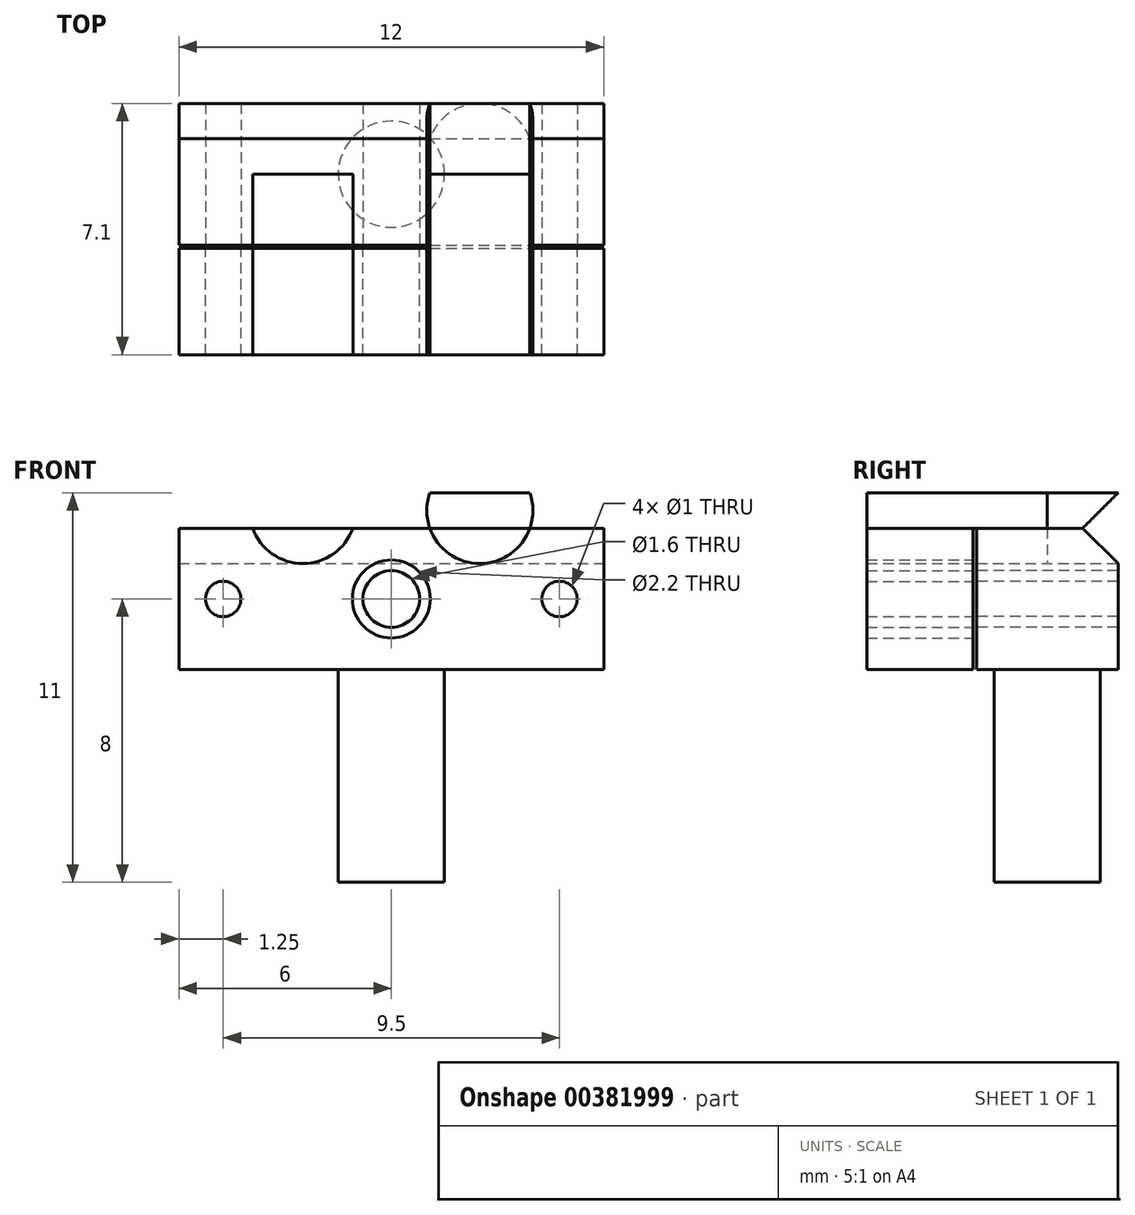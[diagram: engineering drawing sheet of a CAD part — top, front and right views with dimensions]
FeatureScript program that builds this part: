
annotation { "Feature Type Name" : "Feature", "Feature Type Description" : "" }
export const myFeature = defineFeature(function(context is Context, id is Id, definition is map)
    precondition{}
    {
        {
            var Q0;
            Q0=qCreatedBy(makeId("Front.planeOp"),FACE);
            var sketch = newSketch(context, id + "F0", { "sketchPlane" : qUnion([Q0])});
            skArc(sketch, "E0", {"start": v(-1.41, 2) * mm, "mid": v(0, 0) * mm, "end": v(1.41, 2) * mm});
            skLineSegment(sketch, "E1", {"start": v(-1.41, 2) * mm, "end": v(1.41, 2) * mm});
            skLineSegment(sketch, "E2", {"start": v(0, 1.5) * mm, "end": v(0, 0) * mm, "construction": true});
            skArc(sketch, "E3.1.0.0", {"start": v(3.59, 2) * mm, "mid": v(5, 0) * mm, "end": v(6.41, 2) * mm});
            skLineSegment(sketch, "E3.1.0.1", {"start": v(3.59, 2) * mm, "end": v(6.41, 2) * mm});
            skLineSegment(sketch, "E3.direction1", {"start": v(-1.41, 2) * mm, "end": v(3.59, 2) * mm, "construction": true});
            skLineSegment(sketch, "E4", {"start": v(-3.5, 1) * mm, "end": v(8.5, 1) * mm});
            skLineSegment(sketch, "E5", {"start": v(-1.5, 1.5) * mm, "end": v(-1.5, 1) * mm, "construction": true});
            skLineSegment(sketch, "E6", {"start": v(-3.5, 1) * mm, "end": v(-3.5, -3) * mm});
            skLineSegment(sketch, "E7", {"start": v(-3.5, -3) * mm, "end": v(8.5, -3) * mm});
            skLineSegment(sketch, "E8", {"start": v(8.5, -3) * mm, "end": v(8.5, 1) * mm});
            skSolve(sketch);
        }
        {
            var Q0;
            {var subQ0=sQuery(id+"F0.wireOp",EDGE,"E6");Q0=makeQuery(id+"F0.imprint","IMPRINT",FACE,{"disambiguationData":[TD([[makeQuery(id+"F0.imprint","IMPRINT",EDGE,{"derivedFrom":subQ0}),1.0]])]});}
            extrude(context, id + "F1", {"entities" : qUnion([Q0]), "depth" : 2 * mm});
        }
        {
            var Q0;
            {var subQ0=sQuery(id+"F0.wireOp",EDGE,"E6");Q0=makeQuery(id+"F0.imprint","IMPRINT",FACE,{"disambiguationData":[TD([[makeQuery(id+"F0.imprint","IMPRINT",EDGE,{"derivedFrom":subQ0}),1.0]])]});}
            var Q1;
            {var subQ0=sQuery(id+"F0.wireOp",EDGE,"E4");var subQ1=sQuery(id+"F0.wireOp",EDGE,"E3.2.0.0");var subQ2=makeQuery(id+"F0.imprint","INTERSECT",VERTEX,{"disambiguationData":[OD(0.0)],"derivedFrom":[subQ1,subQ0]});Q1=makeQuery(id+"F0.imprint","IMPRINT",FACE,{"disambiguationData":[TD([[makeQuery(id+"F0.imprint","IMPRINT",EDGE,{"disambiguationData":[TD([[subQ2,-1.0]])],"derivedFrom":subQ1}),1.0]])]});}
            var Q2;
            {var subQ0=sQuery(id+"F0.wireOp",EDGE,"E4");var subQ1=sQuery(id+"F0.wireOp",EDGE,"E3.1.0.0");var subQ2=makeQuery(id+"F0.imprint","INTERSECT",VERTEX,{"disambiguationData":[OD(0.0)],"derivedFrom":[subQ1,subQ0]});Q2=makeQuery(id+"F0.imprint","IMPRINT",FACE,{"disambiguationData":[TD([[makeQuery(id+"F0.imprint","IMPRINT",EDGE,{"disambiguationData":[TD([[subQ2,-1.0]])],"derivedFrom":subQ1}),1.0]])]});}
            var Q3;
            {var subQ0=sQuery(id+"F0.wireOp",EDGE,"E4");var subQ1=sQuery(id+"F0.wireOp",EDGE,"E0");var subQ2=makeQuery(id+"F0.imprint","INTERSECT",VERTEX,{"disambiguationData":[OD(0.0)],"derivedFrom":[subQ1,subQ0]});Q3=makeQuery(id+"F0.imprint","IMPRINT",FACE,{"disambiguationData":[TD([[makeQuery(id+"F0.imprint","IMPRINT",EDGE,{"disambiguationData":[TD([[subQ2,-1.0]])],"derivedFrom":subQ1}),1.0]])]});}
            extrude(context, id + "F2", {"entities" : qUnion([Q0, Q1, Q2, Q3]), "operationType" : NewBodyOperationType.ADD, "oppositeDirection" : true, "depth" : 2 * mm});
        }
        {
            var Q0;
            {var subQ0=sQuery(id+"F0.wireOp",EDGE,"E7");Q0=makeQuery(id+"F2.boolean.opBoolean","MERGE",FACE,{"derivedFrom":[makeQuery(id+"F1.opExtrude","SWEPT_FACE",FACE,{"disambiguationData":[OSD([subQ0])]}),makeQuery(id+"F2.opExtrude","SWEPT_FACE",FACE,{"disambiguationData":[OSD([subQ0])]})]});}
            var sketch = newSketch(context, id + "F3", { "sketchPlane" : qUnion([Q0])});
            skLineSegment(sketch, "E9", {"start": v(-3.5, 2) * mm, "end": v(8.5, -2) * mm, "construction": true});
            skCircle(sketch, "E10", {"center": v(2.5, 0) * mm, "radius": 1.5 * mm});
            skSolve(sketch);
        }
        {
            var Q0;
            Q0=makeQuery(id+"F3.imprint","IMPRINT",FACE,{"disambiguationData":[TD([[makeQuery(id+"F3.imprint","IMPRINT",EDGE,{"derivedFrom":sQuery(id+"F3.wireOp",EDGE,"E10")}),1.0]])]});
            extrude(context, id + "F4", {"entities" : qUnion([Q0]), "operationType" : NewBodyOperationType.ADD, "depth" : 6 * mm});
        }
        {
            var Q0;
            Q0=makeQuery(id+"F2.opExtrude","CAP_EDGE",EDGE,{"disambiguationData":[OSD([sQuery(id+"F0.wireOp",EDGE,"E4")])],"isStart":false});
            chamfer(context, id + "F5", {"entities" : qUnion([Q0]), "width" : 1 * mm, "tangentPropagation" : true});
        }
        {
            var Q0;
            {var subQ0=sQuery(id+"F0.wireOp",EDGE,"E4");var subQ1=sQuery(id+"F0.wireOp",EDGE,"E0");var subQ2=makeQuery(id+"F0.imprint","INTERSECT",VERTEX,{"disambiguationData":[OD(0.0)],"derivedFrom":[subQ1,subQ0]});Q0=makeQuery(id+"F0.imprint","IMPRINT",FACE,{"disambiguationData":[TD([[makeQuery(id+"F0.imprint","IMPRINT",EDGE,{"disambiguationData":[TD([[subQ2,-1.0]])],"derivedFrom":subQ1}),1.0]])]});}
            var Q1;
            {var subQ0=sQuery(id+"F0.wireOp",EDGE,"E4");var subQ1=sQuery(id+"F0.wireOp",EDGE,"E3.1.0.0");var subQ2=makeQuery(id+"F0.imprint","INTERSECT",VERTEX,{"disambiguationData":[OD(0.0)],"derivedFrom":[subQ1,subQ0]});Q1=makeQuery(id+"F0.imprint","IMPRINT",FACE,{"disambiguationData":[TD([[makeQuery(id+"F0.imprint","IMPRINT",EDGE,{"disambiguationData":[TD([[subQ2,-1.0]])],"derivedFrom":subQ1}),1.0]])]});}
            var Q2;
            {var subQ0=sQuery(id+"F0.wireOp",EDGE,"E4");var subQ1=sQuery(id+"F0.wireOp",EDGE,"E3.2.0.0");var subQ2=makeQuery(id+"F0.imprint","INTERSECT",VERTEX,{"disambiguationData":[OD(0.0)],"derivedFrom":[subQ1,subQ0]});Q2=makeQuery(id+"F0.imprint","IMPRINT",FACE,{"disambiguationData":[TD([[makeQuery(id+"F0.imprint","IMPRINT",EDGE,{"disambiguationData":[TD([[subQ2,-1.0]])],"derivedFrom":subQ1}),1.0]])]});}
            extrude(context, id + "F6", {"entities" : qUnion([Q0, Q1, Q2]), "depth" : 5.1 * mm});
        }
        {
            var Q0;
            Q0=makeQuery(id+"F1.opExtrude","CAP_FACE",FACE,{"disambiguationData":[OSD([sQuery(id+"F0.wireOp",EDGE,"E0"),sQuery(id+"F0.wireOp",EDGE,"E3.1.0.0"),sQuery(id+"F0.wireOp",EDGE,"E3.2.0.0"),sQuery(id+"F0.wireOp",EDGE,"E4"),sQuery(id+"F0.wireOp",EDGE,"E6"),sQuery(id+"F0.wireOp",EDGE,"E7"),sQuery(id+"F0.wireOp",EDGE,"E8")])],"isStart":false});
            extrude(context, id + "F7", {"entities" : qUnion([Q0]), "depth" : 3 * mm});
        }
        {
            var Q0;
            Q0=makeQuery(id+"F7.opExtrude","SWEPT_BODY",BODY,{"disambiguationData":[OSD([sQuery(id+"F0.wireOp",EDGE,"E0"),sQuery(id+"F0.wireOp",EDGE,"E3.1.0.0"),sQuery(id+"F0.wireOp",EDGE,"E3.2.0.0"),sQuery(id+"F0.wireOp",EDGE,"E4"),sQuery(id+"F0.wireOp",EDGE,"E6"),sQuery(id+"F0.wireOp",EDGE,"E7"),sQuery(id+"F0.wireOp",EDGE,"E8")])]});
            transform(context, id + "F8", {"entities" : qUnion([Q0]), "transformType" : TransformType.TRANSLATION_3D, "dx" : 0 * mm, "dy" : -0.1 * mm, "dz" : 0 * mm, "makeCopy" : false});
        }
        {
            var Q0;
            Q0=makeQuery(id+"F1.opExtrude","CAP_FACE",FACE,{"disambiguationData":[OSD([sQuery(id+"F0.wireOp",EDGE,"E0"),sQuery(id+"F0.wireOp",EDGE,"E3.1.0.0"),sQuery(id+"F0.wireOp",EDGE,"E3.2.0.0"),sQuery(id+"F0.wireOp",EDGE,"E4"),sQuery(id+"F0.wireOp",EDGE,"E6"),sQuery(id+"F0.wireOp",EDGE,"E7"),sQuery(id+"F0.wireOp",EDGE,"E8")])],"isStart":false});
            var sketch = newSketch(context, id + "F9", { "sketchPlane" : qUnion([Q0])});
            skCircle(sketch, "E11", {"center": v(-2.25, -1) * mm, "radius": 0.5 * mm});
            skCircle(sketch, "E12", {"center": v(7.25, -1) * mm, "radius": 0.5 * mm});
            skLineSegment(sketch, "E13", {"start": v(-3.5, 1) * mm, "end": v(8.5, -3) * mm, "construction": true});
            skLineSegment(sketch, "E14", {"start": v(8.5, 1) * mm, "end": v(-3.5, -3) * mm, "construction": true});
            skCircle(sketch, "E15", {"center": v(2.5, -1) * mm, "radius": 0.8 * mm});
            skCircle(sketch, "E16", {"center": v(2.5, -1) * mm, "radius": 1.1 * mm});
            skCircle(sketch, "E17", {"center": v(2.5, -1) * mm, "radius": 1.9 * mm, "construction": true});
            skSolve(sketch);
        }
        {
            var Q0;
            Q0=makeQuery(id+"F9.imprint","IMPRINT",FACE,{"disambiguationData":[TD([[makeQuery(id+"F9.imprint","IMPRINT",EDGE,{"derivedFrom":sQuery(id+"F9.wireOp",EDGE,"E11")}),1.0]])]});
            var Q1;
            Q1=makeQuery(id+"F9.imprint","IMPRINT",FACE,{"disambiguationData":[TD([[makeQuery(id+"F9.imprint","IMPRINT",EDGE,{"derivedFrom":sQuery(id+"F9.wireOp",EDGE,"E12")}),1.0]])]});
            extrude(context, id + "F10", {"entities" : qUnion([Q0, Q1]), "operationType" : NewBodyOperationType.REMOVE, "oppositeDirection" : true, "depth" : 4 * mm});
        }
        {
            var Q0;
            Q0 = qSketchRegion(id + "F9", true);
            var Q1;
            Q1=sQuery(id+"F9.wireOp",EDGE,"E12");
            var Q2;
            Q2=sQuery(id+"F9.wireOp",EDGE,"E11");
            extrude(context, id + "F11", {"entities" : qUnion([Q0]), "operationType" : NewBodyOperationType.REMOVE, "surfaceEntities" : qUnion([Q1, Q2]), "depth" : 3.1 * mm});
        }
        {
            var Q0;
            Q0=makeQuery(id+"F9.imprint","IMPRINT",FACE,{"disambiguationData":[TD([[makeQuery(id+"F9.imprint","IMPRINT",EDGE,{"derivedFrom":sQuery(id+"F9.wireOp",EDGE,"E15")}),1.0]])]});
            var Q1;
            Q1=sQuery(id+"F9.wireOp",EDGE,"E15");
            extrude(context, id + "F12", {"entities" : qUnion([Q0]), "operationType" : NewBodyOperationType.REMOVE, "surfaceEntities" : qUnion([Q1]), "oppositeDirection" : true, "depth" : 4 * mm});
        }
        {
            var Q0;
            Q0=makeQuery(id+"F11.boolean.opBoolean","SPLIT",BODY,{"disambiguationData":[OD(1.0)],"derivedFrom":makeQuery(id+"F6.opExtrude","SWEPT_BODY",BODY,{"disambiguationData":[OSD([sQuery(id+"F0.wireOp",EDGE,"E0"),sQuery(id+"F0.wireOp",EDGE,"E4")])]})});
            deleteBodies(context, id + "F13", {"entities" : qUnion([Q0])});
        }
    });
